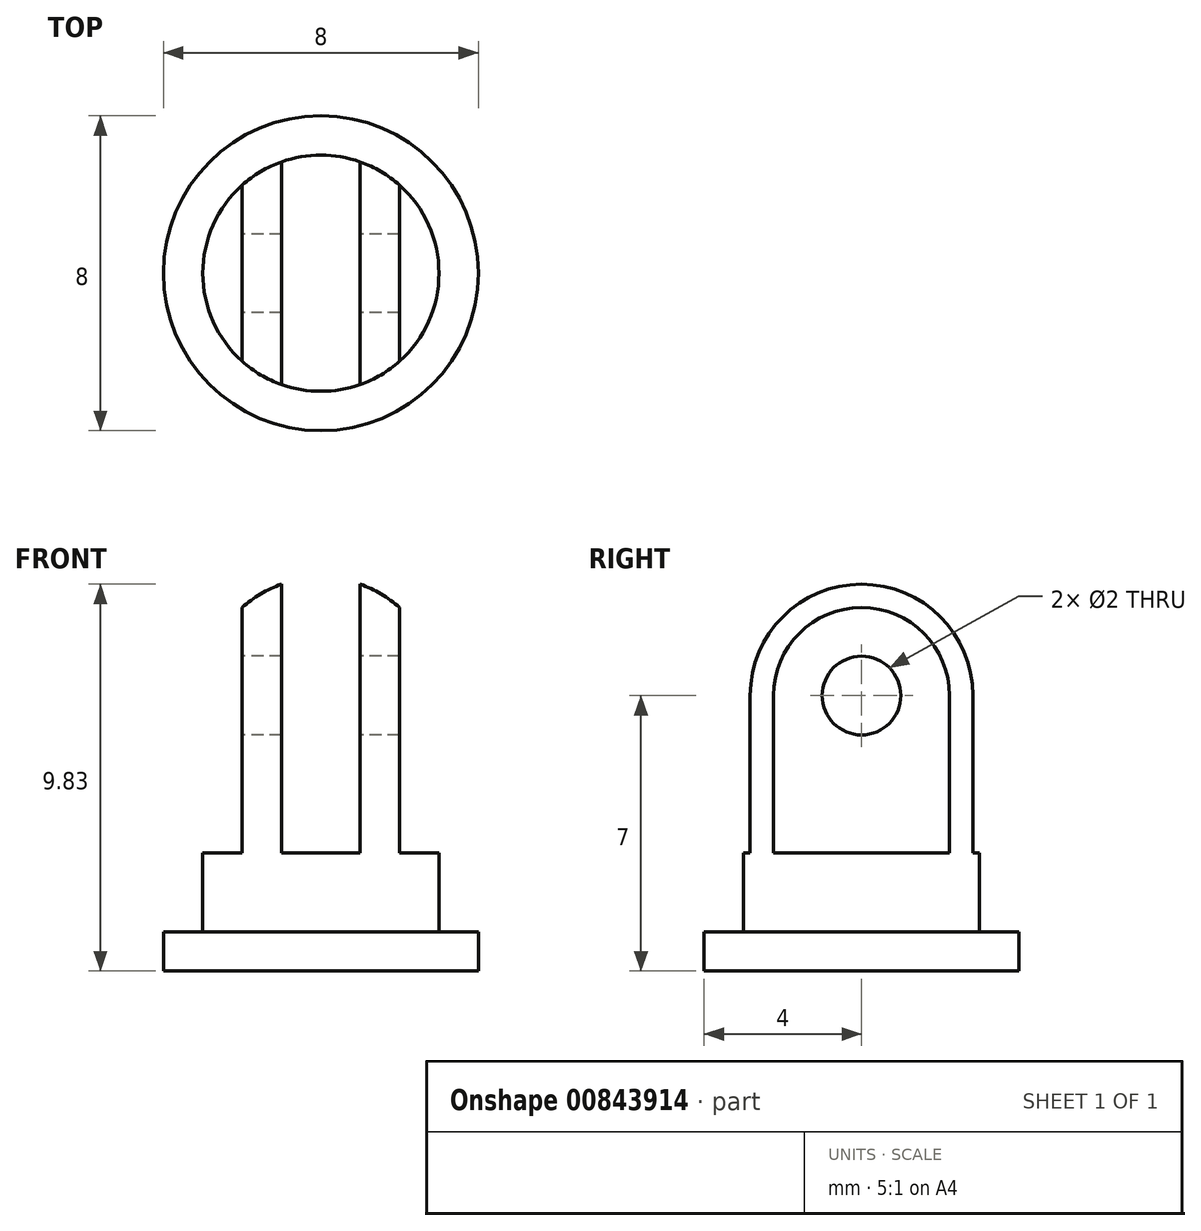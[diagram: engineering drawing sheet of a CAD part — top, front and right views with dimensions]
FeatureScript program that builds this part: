
annotation { "Feature Type Name" : "Feature", "Feature Type Description" : "" }
export const myFeature = defineFeature(function(context is Context, id is Id, definition is map)
    precondition{}
    {
        {
            var Q0;
            Q0=qCreatedBy(makeId("Top.planeOp"),FACE);
            var sketch = newSketch(context, id + "F0", { "sketchPlane" : qUnion([Q0])});
            skCircle(sketch, "E0", {"center": v(0, 0) * mm, "radius": 4 * mm});
            skSolve(sketch);
        }
        {
            var Q0;
            Q0 = qSketchRegion(id + "F0", true);
            extrude(context, id + "F1", {"entities" : qUnion([Q0]), "depth" : 1 * mm, "offsetDistance" : 25 * mm});
        }
        {
            var Q0;
            Q0=makeQuery(id+"F1.opExtrude","CAP_FACE",FACE,{"disambiguationData":[OSD([sQuery(id+"F0.wireOp",EDGE,"E0")])],"isStart":false});
            var sketch = newSketch(context, id + "F2", { "sketchPlane" : qUnion([Q0])});
            skCircle(sketch, "E1", {"center": v(0, 0) * mm, "radius": 3 * mm});
            skSolve(sketch);
        }
        {
            var Q0;
            Q0 = qSketchRegion(id + "F2", true);
            extrude(context, id + "F3", {"entities" : qUnion([Q0]), "operationType" : NewBodyOperationType.ADD, "depth" : 6 * mm, "offsetDistance" : 25 * mm});
        }
        {
            var Q0;
            Q0=qCreatedBy(makeId("Front.planeOp"),FACE);
            var sketch = newSketch(context, id + "F4", { "sketchPlane" : qUnion([Q0])});
            skArc(sketch, "E2", {"start": v(3, 7) * mm, "mid": v(2.12, 9.12) * mm, "end": v(0, 10) * mm});
            skLineSegment(sketch, "E3", {"start": v(0, 10) * mm, "end": v(0, 7) * mm});
            skLineSegment(sketch, "E4", {"start": v(3, 7) * mm, "end": v(0, 7) * mm});
            skSolve(sketch);
        }
        {
            var Q0;
            Q0 = qSketchRegion(id + "F4", true);
            var Q1;
            Q1=sQuery(id+"F4.wireOp",EDGE,"E3");
            revolve(context, id + "F5", {"operationType" : NewBodyOperationType.ADD, "surfaceOperationType" : NewSurfaceOperationType.NEW, "entities" : qUnion([Q0]), "axis" : qUnion([Q1]), "revolveType" : RevolveType.FULL});
        }
        {
            var Q0;
            Q0=qCreatedBy(makeId("Front.planeOp"),FACE);
            var sketch = newSketch(context, id + "F6", { "sketchPlane" : qUnion([Q0])});
            skLineSegment(sketch, "E5.bottom", {"start": v(1, 3) * mm, "end": v(-1, 3) * mm});
            skLineSegment(sketch, "E5.top", {"start": v(1, 15.68) * mm, "end": v(-1, 15.68) * mm});
            skLineSegment(sketch, "E5.left", {"start": v(1, 3) * mm, "end": v(1, 15.68) * mm});
            skLineSegment(sketch, "E5.right", {"start": v(-1, 3) * mm, "end": v(-1, 15.68) * mm});
            skPoint(sketch, "E5.middle", {"position": v(0, 9.34) * mm});
            skLineSegment(sketch, "E6.bottom", {"start": v(3.97, 3) * mm, "end": v(2, 3) * mm});
            skLineSegment(sketch, "E6.top", {"start": v(3.97, 15.97) * mm, "end": v(2, 15.97) * mm});
            skLineSegment(sketch, "E6.left", {"start": v(3.97, 3) * mm, "end": v(3.97, 15.97) * mm});
            skLineSegment(sketch, "E6.right", {"start": v(2, 3) * mm, "end": v(2, 15.97) * mm});
            skPoint(sketch, "E6.middle", {"position": v(2.99, 9.49) * mm});
            skLineSegment(sketch, "E7.bottom", {"start": v(-2, 3) * mm, "end": v(-3.88, 3) * mm});
            skLineSegment(sketch, "E7.top", {"start": v(-2, 14.89) * mm, "end": v(-3.88, 14.89) * mm});
            skLineSegment(sketch, "E7.left", {"start": v(-2, 3) * mm, "end": v(-2, 14.89) * mm});
            skLineSegment(sketch, "E7.right", {"start": v(-3.88, 3) * mm, "end": v(-3.88, 14.89) * mm});
            skPoint(sketch, "E7.middle", {"position": v(-2.94, 8.94) * mm});
            skSolve(sketch);
        }
        {
            var Q0;
            Q0 = qSketchRegion(id + "F6", true);
            extrude(context, id + "F7", {"entities" : qUnion([Q0]), "operationType" : NewBodyOperationType.REMOVE, "endBound" : BoundingType.SYMMETRIC, "depth" : 25 * mm, "offsetDistance" : 25 * mm});
        }
        {
            var Q0;
            Q0=makeQuery(id+"F7.boolean.opBoolean","COPY",FACE,{"derivedFrom":makeQuery(id+"F7.opExtrude","SWEPT_FACE",FACE,{"disambiguationData":[OSD([sQuery(id+"F6.wireOp",EDGE,"E7.left")])]})});
            var sketch = newSketch(context, id + "F8", { "sketchPlane" : qUnion([Q0])});
            skCircle(sketch, "E8", {"center": v(0, 7) * mm, "radius": 1 * mm});
            skSolve(sketch);
        }
        {
            var Q0;
            Q0 = qSketchRegion(id + "F8", true);
            extrude(context, id + "F9", {"entities" : qUnion([Q0]), "operationType" : NewBodyOperationType.REMOVE, "endBound" : BoundingType.THROUGH_ALL, "oppositeDirection" : true, "depth" : 25 * mm, "offsetDistance" : 25 * mm});
        }
    });
